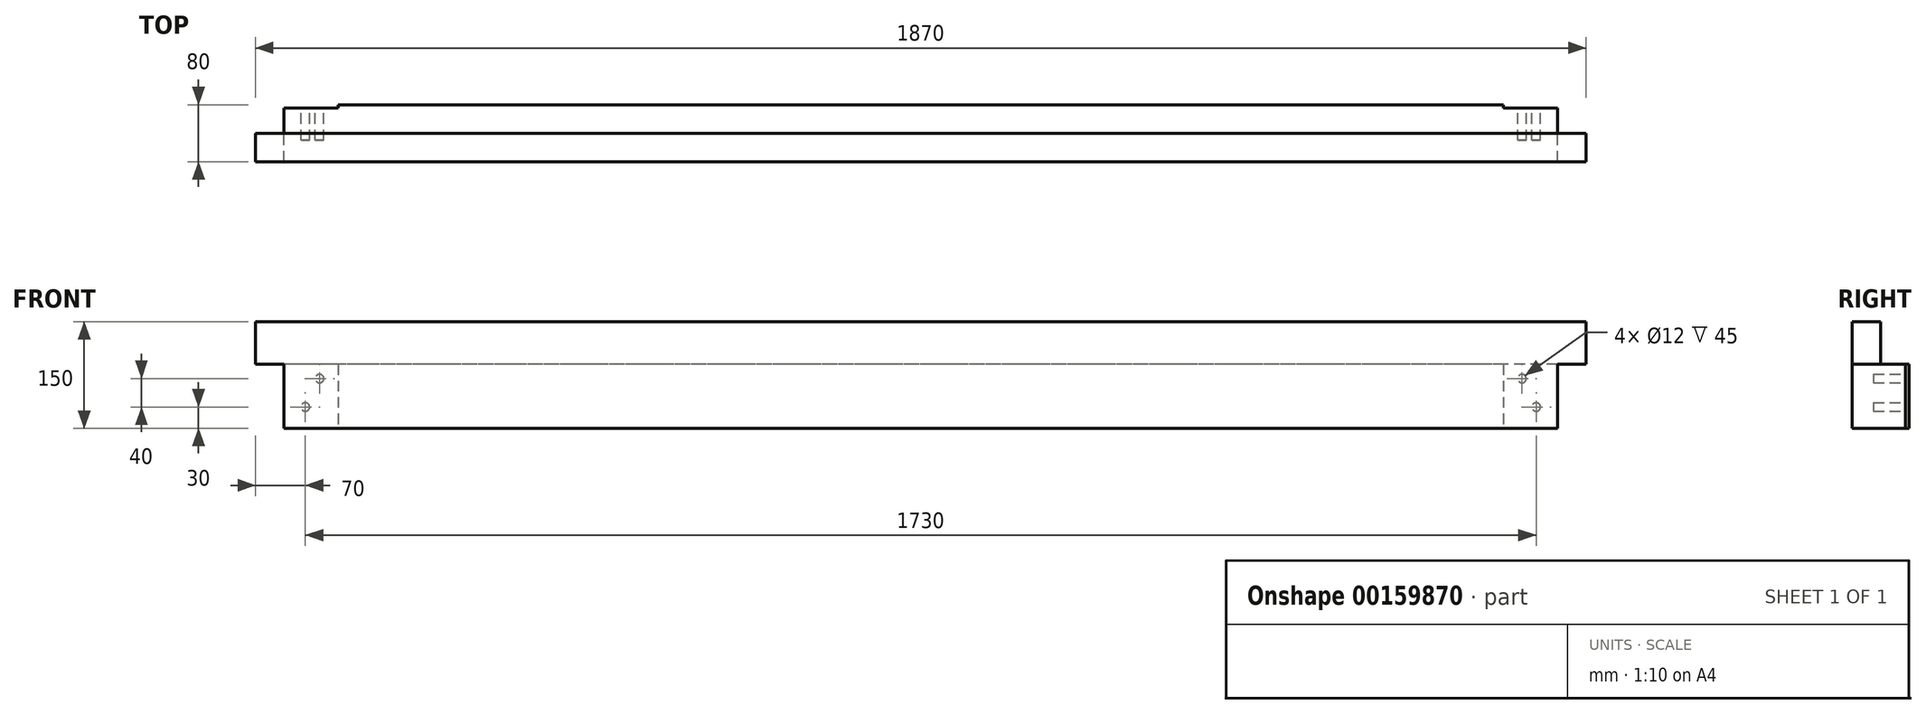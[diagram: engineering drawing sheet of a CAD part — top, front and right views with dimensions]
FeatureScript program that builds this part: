
annotation { "Feature Type Name" : "Feature", "Feature Type Description" : "" }
export const myFeature = defineFeature(function(context is Context, id is Id, definition is map)
    precondition{}
    {
        {
            assignVariable(context, id + "F0", {"name" : "B", "anyValue" : 80 * mm});
        }
        {
            assignVariable(context, id + "F1", {"name" : "L", "anyValue" : 1790 * mm});
        }
        {
            var Q0;
            Q0=qCreatedBy(makeId("Right.planeOp"),FACE);
            var sketch = newSketch(context, id + "F2", { "sketchPlane" : qUnion([Q0])});
            skLineSegment(sketch, "E0.bottom", {"start": v(-40, -75) * mm, "end": v(40, -75) * mm});
            skLineSegment(sketch, "E0.top", {"start": v(-40, 75) * mm, "end": v(0, 75) * mm});
            skLineSegment(sketch, "E0.left", {"start": v(-40, -75) * mm, "end": v(-40, 75) * mm});
            skLineSegment(sketch, "E0.right", {"start": v(40, -75) * mm, "end": v(40, 15) * mm});
            skPoint(sketch, "E0.middle", {"position": v(0, 0) * mm});
            skLineSegment(sketch, "E1", {"start": v(0, 75) * mm, "end": v(0, 15) * mm});
            skLineSegment(sketch, "E2", {"start": v(0, 15) * mm, "end": v(40, 15) * mm});
            skSolve(sketch);
        }
        {
            var Q0;
            Q0=qSketchRegion(id+"F2",true);
            extrude(context, id + "F3", {"entities" : qUnion([Q0]), "endBound" : BoundingType.SYMMETRIC, "depth" : getVariable(context, 'L')});
        }
        {
            var Q0;
            Q0=makeQuery(id+"F3.opExtrude","SWEPT_FACE",FACE,{"disambiguationData":[OSD([sQuery(id+"F2.wireOp",EDGE,"E0.right")])]});
            var sketch = newSketch(context, id + "F4", { "sketchPlane" : qUnion([Q0])});
            skCircle(sketch, "E3", {"center": v(-865, -45) * mm, "radius": 6 * mm});
            skCircle(sketch, "E4", {"center": v(-845, -5) * mm, "radius": 6 * mm});
            skCircle(sketch, "E5.MirrorC", {"center": v(845, -5) * mm, "radius": 6 * mm});
            skCircle(sketch, "E6.MirrorC", {"center": v(865, -45) * mm, "radius": 6 * mm});
            skSolve(sketch);
        }
        {
            var Q0;
            Q0=qSketchRegion(id+"F4",true);
            extrude(context, id + "F5", {"entities" : qUnion([Q0]), "operationType" : NewBodyOperationType.REMOVE, "oppositeDirection" : true, "depth" : getVariable(context, 'B') - 30 * mm});
        }
        {
            var Q0;
            Q0=makeQuery(id+"F3.opExtrude","SWEPT_FACE",FACE,{"disambiguationData":[OSD([sQuery(id+"F2.wireOp",EDGE,"E0.right")])]});
            var sketch = newSketch(context, id + "F6", { "sketchPlane" : qUnion([Q0])});
            skLineSegment(sketch, "E7.bottom", {"start": v(-819, 15) * mm, "end": v(-895, 15) * mm});
            skLineSegment(sketch, "E7.top", {"start": v(-819, -75) * mm, "end": v(-895, -75) * mm});
            skLineSegment(sketch, "E7.left", {"start": v(-819, 15) * mm, "end": v(-819, -75) * mm});
            skLineSegment(sketch, "E7.right", {"start": v(-895, 15) * mm, "end": v(-895, -75) * mm});
            skLineSegment(sketch, "E8.MirrorCS", {"start": v(895, 15) * mm, "end": v(895, -75) * mm});
            skLineSegment(sketch, "E9.MirrorCS", {"start": v(819, 15) * mm, "end": v(895, 15) * mm});
            skLineSegment(sketch, "E10.MirrorCS", {"start": v(819, 15) * mm, "end": v(819, -75) * mm});
            skLineSegment(sketch, "E11.MirrorCS", {"start": v(819, -75) * mm, "end": v(895, -75) * mm});
            skSolve(sketch);
        }
        {
            var Q0;
            Q0=qSketchRegion(id+"F6",true);
            extrude(context, id + "F7", {"entities" : qUnion([Q0]), "operationType" : NewBodyOperationType.REMOVE, "oppositeDirection" : true, "depth" : 5 * mm});
        }
        {
            var Q0;
            Q0=qCreatedBy(makeId("Right.planeOp"),FACE);
            var sketch = newSketch(context, id + "F8", { "sketchPlane" : qUnion([Q0])});
            skLineSegment(sketch, "E12.bottom", {"start": v(0, 15) * mm, "end": v(-40, 15) * mm});
            skLineSegment(sketch, "E12.top", {"start": v(0, 75) * mm, "end": v(-40, 75) * mm});
            skLineSegment(sketch, "E12.left", {"start": v(0, 15) * mm, "end": v(0, 75) * mm});
            skLineSegment(sketch, "E12.right", {"start": v(-40, 15) * mm, "end": v(-40, 75) * mm});
            skSolve(sketch);
        }
        {
            var Q0;
            Q0 = qSketchRegion(id + "F8", true);
            extrude(context, id + "F9", {"entities" : qUnion([Q0]), "operationType" : NewBodyOperationType.ADD, "endBound" : BoundingType.SYMMETRIC, "depth" : 40 * mm * 2 + getVariable(context, 'L')});
        }
    });
